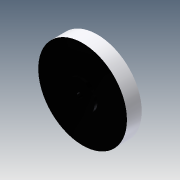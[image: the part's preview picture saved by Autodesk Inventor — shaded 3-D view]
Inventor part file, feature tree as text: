
AUTODESK INVENTOR PART (.ipt)
format: ipt  version: 2014 (Build 180170000, 170)  size: 93,184 bytes
history: native  units: in
note: dims shown in document units (in); Inventor stores cm internally (conversion verified against a paired STEP export)
features: extrude x3, sketch x3
ambient origin geometry x8: Origin, YZ Plane, XZ Plane, XY Plane, X Axis, Y Axis, Z Axis, Center Point
bodies: Solid1 (feature_tree)
feature tree (6):
  extrude  "Extrusion1"  Depth=1.0in TaperAngle=0.0deg
  extrude  "Extrusion2"  Depth=0.1875in TaperAngle=0.0deg
  extrude  "Extrusion3"  Depth=1.375in TaperAngle=0.0deg
  sketch  "Sketch1"  dims[d0=6.0in d1=1.0in d2=0.0in]
  sketch  "Sketch2"  dims[d3=2.0in d4=0.1875in d5=1.1875in d6=0.0in d7=0.0in]
  sketch  "Sketch3"  dims[d8=0.375in d9=1.375in d10=0.0in]
